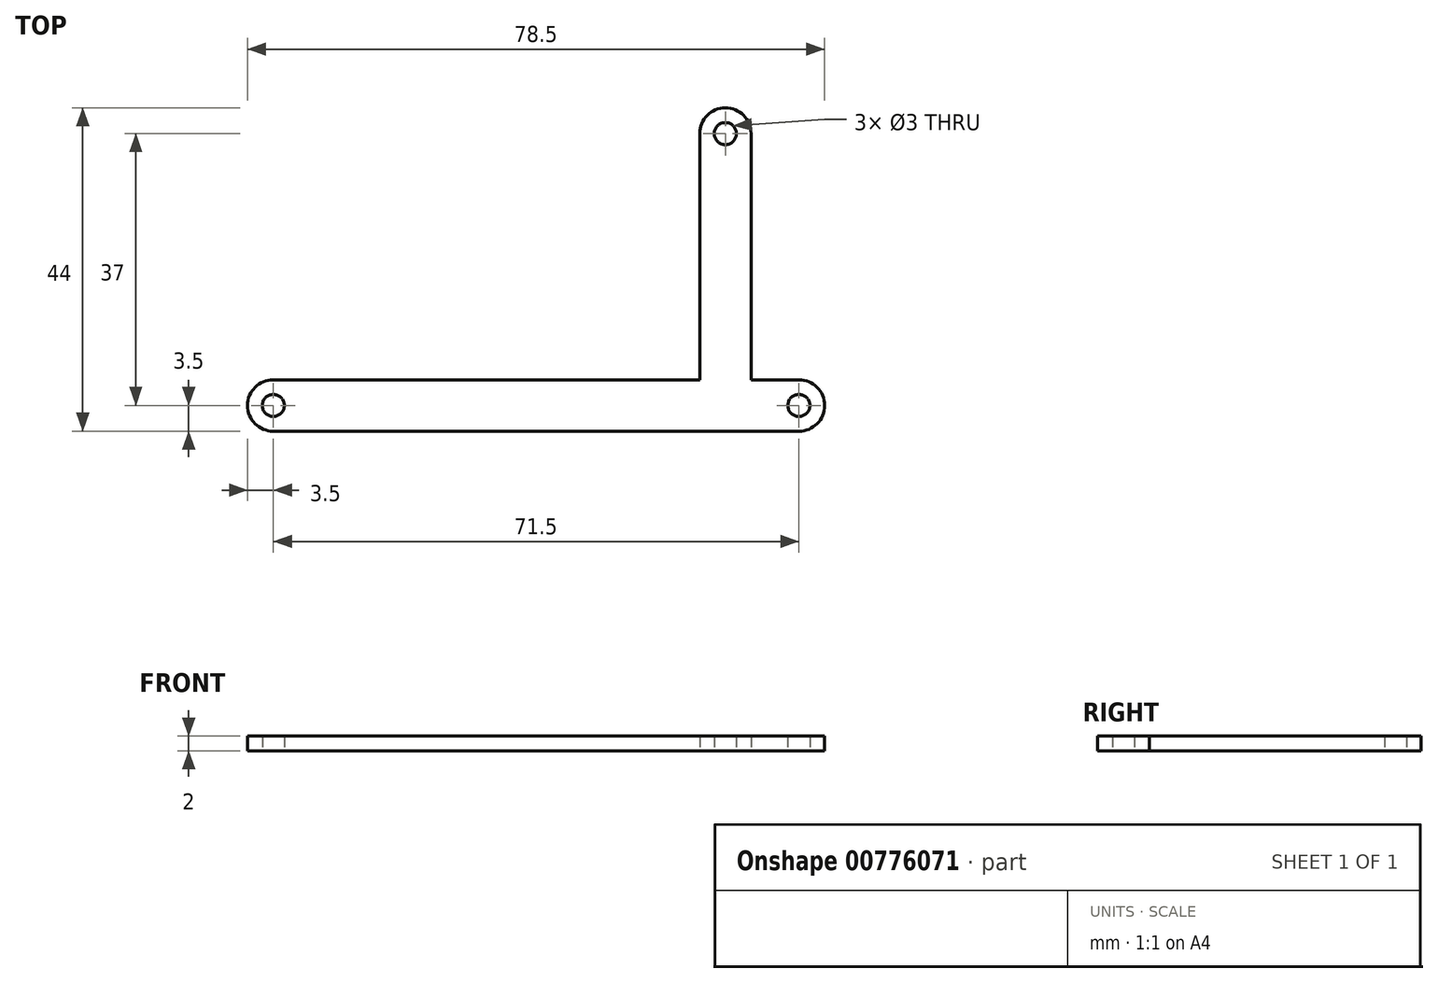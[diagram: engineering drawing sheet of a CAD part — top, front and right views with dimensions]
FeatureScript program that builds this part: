
annotation { "Feature Type Name" : "Feature", "Feature Type Description" : "" }
export const myFeature = defineFeature(function(context is Context, id is Id, definition is map)
    precondition{}
    {
        {
            var Q0;
            Q0=qCreatedBy(makeId("Top.planeOp"),FACE);
            var sketch = newSketch(context, id + "F0", { "sketchPlane" : qUnion([Q0])});
            skCircle(sketch, "E0", {"center": v(0, 0) * mm, "radius": 1.5 * mm});
            skCircle(sketch, "E1", {"center": v(71.5, 0) * mm, "radius": 1.5 * mm});
            skCircle(sketch, "E2", {"center": v(61.5, 37) * mm, "radius": 1.5 * mm});
            skArc(sketch, "E3.0", {"start": v(65, 37) * mm, "mid": v(61.5, 40.5) * mm, "end": v(58, 37) * mm});
            skArc(sketch, "E4.0", {"start": v(71.5, -3.5) * mm, "mid": v(75, 0) * mm, "end": v(71.5, 3.5) * mm});
            skArc(sketch, "E5.0", {"start": v(0, 3.5) * mm, "mid": v(-3.5, 0) * mm, "end": v(0, -3.5) * mm});
            skLineSegment(sketch, "E6", {"start": v(0, 3.5) * mm, "end": v(58, 3.5) * mm});
            skLineSegment(sketch, "E7", {"start": v(0, -3.5) * mm, "end": v(71.5, -3.5) * mm});
            skLineSegment(sketch, "E8", {"start": v(58, 37) * mm, "end": v(58, 3.5) * mm});
            skLineSegment(sketch, "E9", {"start": v(65, 37) * mm, "end": v(65, 3.5) * mm});
            skLineSegment(sketch, "E10.trimOffspring", {"start": v(65, 3.5) * mm, "end": v(71.5, 3.5) * mm});
            skSolve(sketch);
        }
        {
            var Q0;
            Q0=makeQuery(id+"F0.imprint","IMPRINT",FACE,{"disambiguationData":[TD([[makeQuery(id+"F0.imprint","IMPRINT",EDGE,{"derivedFrom":sQuery(id+"F0.wireOp",EDGE,"E0")}),-1.0]])]});
            extrude(context, id + "F1", {"entities" : qUnion([Q0]), "depth" : 2 * mm, "offsetDistance" : 25 * mm});
        }
    });
